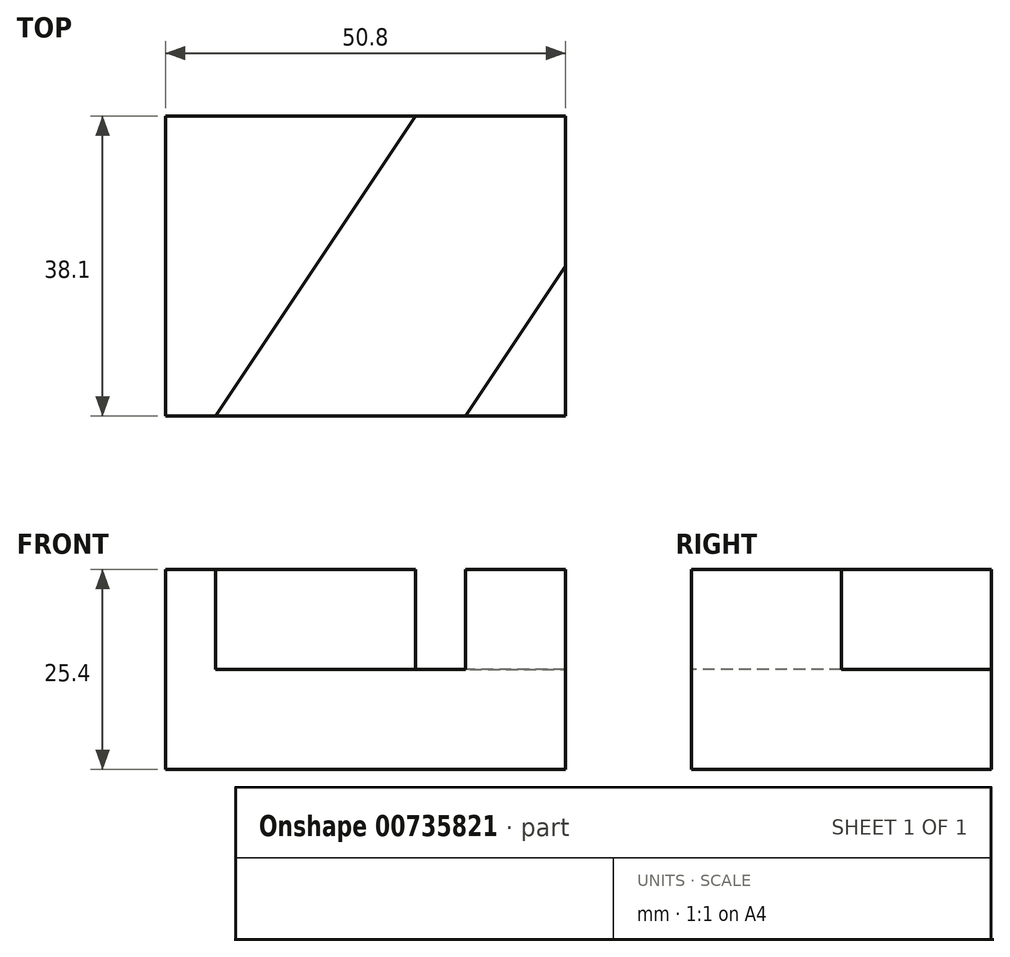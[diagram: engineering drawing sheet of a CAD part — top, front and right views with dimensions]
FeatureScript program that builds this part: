
annotation { "Feature Type Name" : "Feature", "Feature Type Description" : "" }
export const myFeature = defineFeature(function(context is Context, id is Id, definition is map)
    precondition{}
    {
        {
            var Q0;
            Q0=qCreatedBy(makeId("Top.planeOp"),FACE);
            var sketch = newSketch(context, id + "F0", { "sketchPlane" : qUnion([Q0])});
            skLineSegment(sketch, "E0", {"start": v(0, 0) * mm, "end": v(0, 38.1) * mm});
            skLineSegment(sketch, "E1", {"start": v(0, 38.1) * mm, "end": v(50.8, 38.1) * mm});
            skLineSegment(sketch, "E2", {"start": v(50.8, 38.1) * mm, "end": v(50.8, 0) * mm});
            skLineSegment(sketch, "E3", {"start": v(50.8, 0) * mm, "end": v(0, 0) * mm});
            skSolve(sketch);
        }
        {
            var Q0;
            Q0 = qSketchRegion(id + "F0", true);
            extrude(context, id + "F1", {"entities" : qUnion([Q0]), "depth" : 12.7 * mm, "offsetDistance" : 25.4 * mm});
        }
        {
            var Q0;
            Q0=makeQuery(id+"F1.opExtrude","CAP_FACE",FACE,{"disambiguationData":[OSD([sQuery(id+"F0.wireOp",EDGE,"E0"),sQuery(id+"F0.wireOp",EDGE,"E1"),sQuery(id+"F0.wireOp",EDGE,"E2"),sQuery(id+"F0.wireOp",EDGE,"E3")])],"isStart":false});
            var sketch = newSketch(context, id + "F2", { "sketchPlane" : qUnion([Q0])});
            skLineSegment(sketch, "E4", {"start": v(31.75, 38.1) * mm, "end": v(0, 38.1) * mm});
            skLineSegment(sketch, "E5", {"start": v(0, 38.1) * mm, "end": v(0, 0) * mm});
            skLineSegment(sketch, "E6", {"start": v(0, 0) * mm, "end": v(6.35, 0) * mm});
            skLineSegment(sketch, "E7", {"start": v(6.35, 0) * mm, "end": v(31.75, 38.1) * mm});
            skSolve(sketch);
        }
        {
            var Q0;
            Q0 = qSketchRegion(id + "F2", true);
            extrude(context, id + "F3", {"entities" : qUnion([Q0]), "operationType" : NewBodyOperationType.ADD, "depth" : 12.7 * mm, "offsetDistance" : 25.4 * mm});
        }
        {
            var Q0;
            Q0=makeQuery(id+"F1.opExtrude","CAP_FACE",FACE,{"disambiguationData":[OSD([sQuery(id+"F0.wireOp",EDGE,"E0"),sQuery(id+"F0.wireOp",EDGE,"E1"),sQuery(id+"F0.wireOp",EDGE,"E2"),sQuery(id+"F0.wireOp",EDGE,"E3")])],"isStart":false});
            var sketch = newSketch(context, id + "F4", { "sketchPlane" : qUnion([Q0])});
            skLineSegment(sketch, "E8", {"start": v(50.8, 0) * mm, "end": v(50.8, 19.05) * mm});
            skLineSegment(sketch, "E9", {"start": v(50.8, 19.05) * mm, "end": v(38.1, 0) * mm});
            skLineSegment(sketch, "E10", {"start": v(38.1, 0) * mm, "end": v(50.8, 0) * mm});
            skSolve(sketch);
        }
        {
            var Q0;
            Q0 = qSketchRegion(id + "F4", true);
            extrude(context, id + "F5", {"entities" : qUnion([Q0]), "operationType" : NewBodyOperationType.ADD, "depth" : 12.7 * mm, "offsetDistance" : 25.4 * mm});
        }
    });
